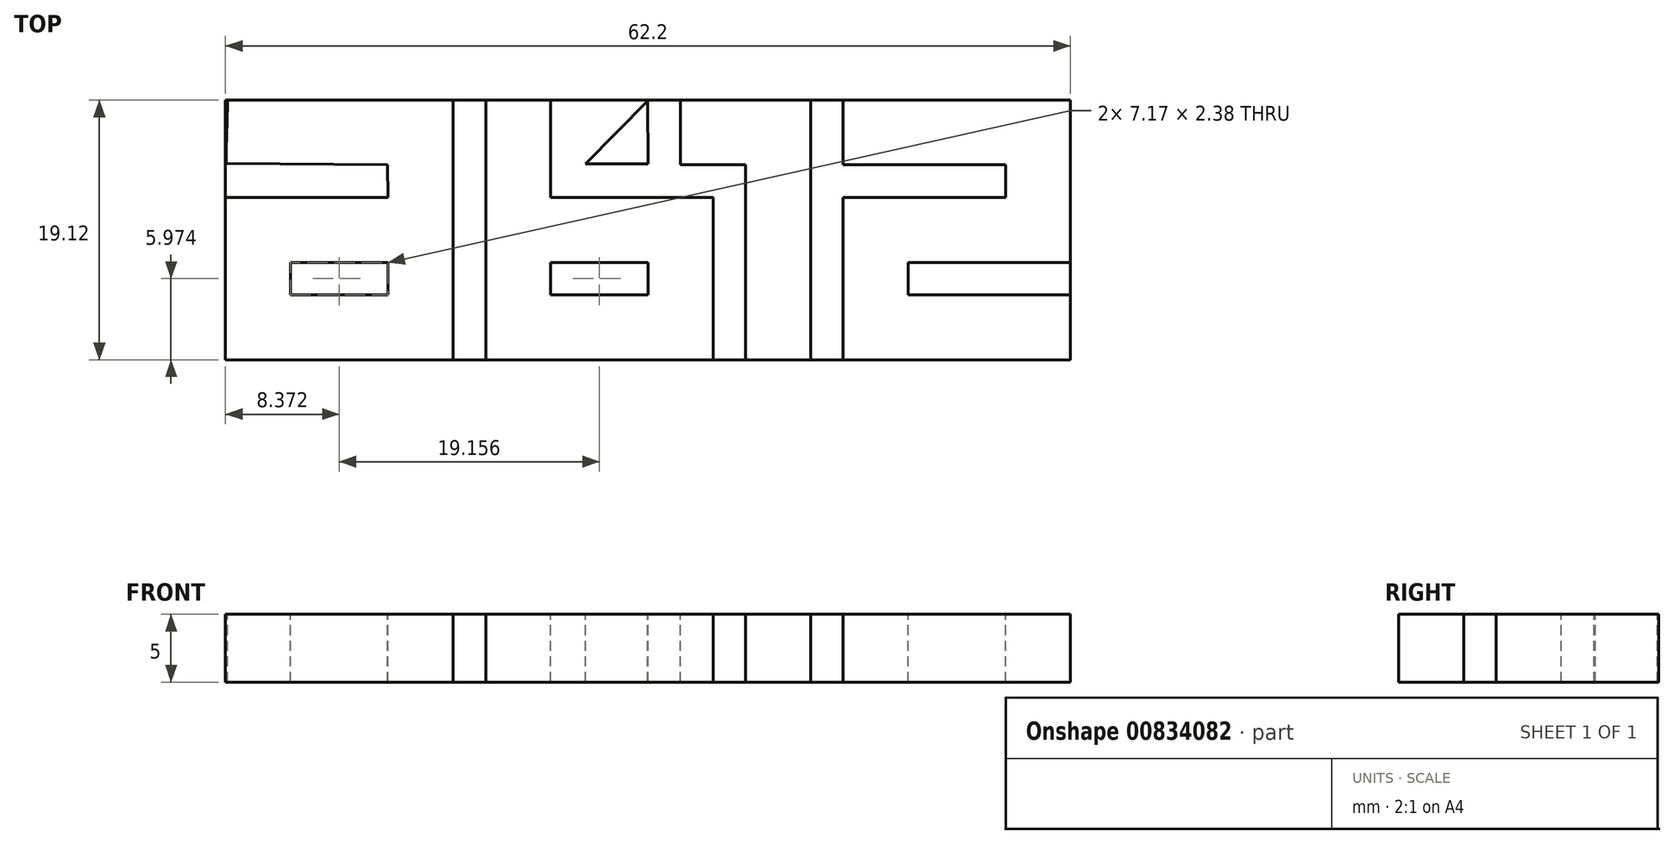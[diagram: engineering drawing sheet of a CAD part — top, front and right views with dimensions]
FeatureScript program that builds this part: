
annotation { "Feature Type Name" : "Feature", "Feature Type Description" : "" }
export const myFeature = defineFeature(function(context is Context, id is Id, definition is map)
    precondition{}
    {
        {
            var Q0;
            Q0=qCreatedBy(makeId("Top.planeOp"),FACE);
            var sketch = newSketch(context, id + "F0", { "sketchPlane" : qUnion([Q0])});
            skLineSegment(sketch, "E0", {"start": v(-31.1, 9.52) * mm, "end": v(-14.35, 9.52) * mm});
            skLineSegment(sketch, "E1", {"start": v(-14.35, 9.52) * mm, "end": v(-14.35, -9.6) * mm});
            skLineSegment(sketch, "E2", {"start": v(-14.35, -9.6) * mm, "end": v(-31.1, -9.6) * mm});
            skLineSegment(sketch, "E3", {"start": v(-31.1, -9.6) * mm, "end": v(-31.1, 2.35) * mm});
            skLineSegment(sketch, "E4", {"start": v(-31.1, 2.35) * mm, "end": v(-19.14, 2.35) * mm});
            skLineSegment(sketch, "E5", {"start": v(-19.14, 2.35) * mm, "end": v(-19.18, 4.77) * mm});
            skLineSegment(sketch, "E6", {"start": v(-19.18, 4.77) * mm, "end": v(-31.06, 4.87) * mm});
            skLineSegment(sketch, "E7", {"start": v(-19.14, -2.44) * mm, "end": v(-26.31, -2.44) * mm});
            skLineSegment(sketch, "E8", {"start": v(-26.31, -2.44) * mm, "end": v(-26.31, -4.82) * mm});
            skLineSegment(sketch, "E9", {"start": v(-26.31, -4.82) * mm, "end": v(-19.14, -4.82) * mm});
            skLineSegment(sketch, "E10", {"start": v(-19.14, -4.82) * mm, "end": v(-19.14, -2.44) * mm});
            skLineSegment(sketch, "E11", {"start": v(-11.95, 9.52) * mm, "end": v(-7.16, 9.52) * mm});
            skLineSegment(sketch, "E12", {"start": v(-7.16, 9.52) * mm, "end": v(-7.16, 2.35) * mm});
            skLineSegment(sketch, "E13", {"start": v(-7.16, 2.35) * mm, "end": v(4.8, 2.35) * mm});
            skLineSegment(sketch, "E14", {"start": v(4.8, 2.35) * mm, "end": v(4.8, -9.6) * mm});
            skLineSegment(sketch, "E15", {"start": v(4.8, -9.6) * mm, "end": v(-11.95, -9.6) * mm});
            skLineSegment(sketch, "E16", {"start": v(-11.95, -9.6) * mm, "end": v(-11.95, 9.52) * mm});
            skLineSegment(sketch, "E17", {"start": v(0.01, -2.44) * mm, "end": v(-7.16, -2.44) * mm});
            skLineSegment(sketch, "E18", {"start": v(-7.16, -2.44) * mm, "end": v(-7.16, -4.82) * mm});
            skLineSegment(sketch, "E19", {"start": v(-7.16, -4.82) * mm, "end": v(0.01, -4.82) * mm});
            skLineSegment(sketch, "E20", {"start": v(0.01, -4.82) * mm, "end": v(0.01, -2.44) * mm});
            skLineSegment(sketch, "E21", {"start": v(7.18, 4.76) * mm, "end": v(7.18, -9.6) * mm});
            skLineSegment(sketch, "E22", {"start": v(7.18, -9.6) * mm, "end": v(11.97, -9.6) * mm});
            skLineSegment(sketch, "E23", {"start": v(11.97, -9.6) * mm, "end": v(11.97, 9.52) * mm});
            skLineSegment(sketch, "E24", {"start": v(11.97, 9.52) * mm, "end": v(2.4, 9.52) * mm});
            skLineSegment(sketch, "E25", {"start": v(2.4, 9.52) * mm, "end": v(2.4, 4.76) * mm});
            skLineSegment(sketch, "E26", {"start": v(2.4, 4.76) * mm, "end": v(7.18, 4.76) * mm});
            skLineSegment(sketch, "E27", {"start": v(31.1, -2.44) * mm, "end": v(19.14, -2.44) * mm});
            skLineSegment(sketch, "E28", {"start": v(19.14, -2.44) * mm, "end": v(19.14, -4.82) * mm});
            skLineSegment(sketch, "E29", {"start": v(19.14, -4.82) * mm, "end": v(31.1, -4.82) * mm});
            skLineSegment(sketch, "E30", {"start": v(31.1, -4.82) * mm, "end": v(31.1, -9.6) * mm});
            skLineSegment(sketch, "E31", {"start": v(31.1, -9.6) * mm, "end": v(14.35, -9.6) * mm});
            skLineSegment(sketch, "E32", {"start": v(14.35, -9.6) * mm, "end": v(14.35, 2.35) * mm});
            skLineSegment(sketch, "E33", {"start": v(14.35, 2.35) * mm, "end": v(26.34, 2.35) * mm});
            skLineSegment(sketch, "E34", {"start": v(26.34, 2.35) * mm, "end": v(26.34, 4.76) * mm});
            skLineSegment(sketch, "E35", {"start": v(26.34, 4.76) * mm, "end": v(14.35, 4.76) * mm});
            skLineSegment(sketch, "E36", {"start": v(14.35, 4.76) * mm, "end": v(14.35, 9.52) * mm});
            skLineSegment(sketch, "E37", {"start": v(14.35, 9.52) * mm, "end": v(31.1, 9.52) * mm});
            skLineSegment(sketch, "E38", {"start": v(31.1, 9.52) * mm, "end": v(31.1, -2.44) * mm});
            skLineSegment(sketch, "E39", {"start": v(-30.95, 9.6) * mm, "end": v(-30.96, 9.21) * mm});
            skLineSegment(sketch, "E40", {"start": v(-30.96, 9.21) * mm, "end": v(-31, 8.03) * mm});
            skLineSegment(sketch, "E41", {"start": v(-31, 8.03) * mm, "end": v(-31.01, 6.85) * mm});
            skLineSegment(sketch, "E42", {"start": v(-31.01, 6.85) * mm, "end": v(-31.03, 6) * mm});
            skLineSegment(sketch, "E43", {"start": v(-31.03, 6) * mm, "end": v(-31.05, 5.44) * mm});
            skLineSegment(sketch, "E44", {"start": v(-31.05, 5.44) * mm, "end": v(-31.05, 5.1) * mm});
            skLineSegment(sketch, "E45", {"start": v(-31.05, 5.1) * mm, "end": v(-31.06, 4.94) * mm});
            skLineSegment(sketch, "E46", {"start": v(-31.06, 4.94) * mm, "end": v(-31.06, 4.88) * mm});
            skLineSegment(sketch, "E47", {"start": v(-31.06, 4.88) * mm, "end": v(-31.06, 4.87) * mm});
            skLineSegment(sketch, "E48", {"start": v(0.01, 4.85) * mm, "end": v(-0.02, 9.45) * mm});
            skLineSegment(sketch, "E49", {"start": v(-0.02, 9.45) * mm, "end": v(-4.6, 4.84) * mm});
            skLineSegment(sketch, "E50", {"start": v(-4.6, 4.84) * mm, "end": v(0.01, 4.85) * mm});
            skSolve(sketch);
        }
        {
            var Q0;
            Q0=makeQuery(id+"F0.imprint","IMPRINT",FACE,{"disambiguationData":[TD([[makeQuery(id+"F0.imprint","IMPRINT",EDGE,{"derivedFrom":sQuery(id+"F0.wireOp",EDGE,"E27")}),-1.0]])]});
            var Q1;
            Q1=makeQuery(id+"F0.imprint","IMPRINT",FACE,{"disambiguationData":[TD([[makeQuery(id+"F0.imprint","IMPRINT",EDGE,{"derivedFrom":sQuery(id+"F0.wireOp",EDGE,"E21")}),1.0]])]});
            var Q2;
            Q2=makeQuery(id+"F0.imprint","IMPRINT",FACE,{"disambiguationData":[TD([[makeQuery(id+"F0.imprint","IMPRINT",EDGE,{"derivedFrom":sQuery(id+"F0.wireOp",EDGE,"E48")}),1.0]])]});
            var Q3;
            Q3=makeQuery(id+"F0.imprint","IMPRINT",FACE,{"disambiguationData":[TD([[makeQuery(id+"F0.imprint","IMPRINT",EDGE,{"derivedFrom":sQuery(id+"F0.wireOp",EDGE,"E11")}),-1.0]])]});
            var Q4;
            {var subQ0=sQuery(id+"F0.wireOp",EDGE,"E1");Q4=makeQuery(id+"F0.imprint","IMPRINT",FACE,{"disambiguationData":[TD([[makeQuery(id+"F0.imprint","IMPRINT",EDGE,{"derivedFrom":subQ0}),-1.0]])]});}
            var Q5;
            Q5=sQuery(id+"F0.wireOp",EDGE,"E31");
            var Q6;
            Q6=sQuery(id+"F0.wireOp",EDGE,"E32");
            var Q7;
            Q7=sQuery(id+"F0.wireOp",EDGE,"E17");
            var Q8;
            Q8=sQuery(id+"F0.wireOp",EDGE,"E27");
            var Q9;
            Q9=sQuery(id+"F0.wireOp",EDGE,"E23");
            var Q10;
            Q10=sQuery(id+"F0.wireOp",EDGE,"E0");
            var Q11;
            Q11=sQuery(id+"F0.wireOp",EDGE,"E9");
            var Q12;
            Q12=sQuery(id+"F0.wireOp",EDGE,"E30");
            var Q13;
            Q13=sQuery(id+"F0.wireOp",EDGE,"E36");
            var Q14;
            Q14=sQuery(id+"F0.wireOp",EDGE,"E33");
            var Q15;
            Q15=sQuery(id+"F0.wireOp",EDGE,"E13");
            var Q16;
            Q16=sQuery(id+"F0.wireOp",EDGE,"E16");
            var Q17;
            Q17=sQuery(id+"F0.wireOp",EDGE,"E15");
            var Q18;
            Q18=sQuery(id+"F0.wireOp",EDGE,"E21");
            var Q19;
            Q19=sQuery(id+"F0.wireOp",EDGE,"E2");
            var Q20;
            Q20=sQuery(id+"F0.wireOp",EDGE,"E24");
            var Q21;
            Q21=sQuery(id+"F0.wireOp",EDGE,"E29");
            var Q22;
            Q22=sQuery(id+"F0.wireOp",EDGE,"E26");
            var Q23;
            Q23=sQuery(id+"F0.wireOp",EDGE,"E4");
            var Q24;
            Q24=sQuery(id+"F0.wireOp",EDGE,"E19");
            var Q25;
            Q25=sQuery(id+"F0.wireOp",EDGE,"E11");
            var Q26;
            Q26=sQuery(id+"F0.wireOp",EDGE,"E14");
            var Q27;
            Q27=sQuery(id+"F0.wireOp",EDGE,"E6");
            var Q28;
            Q28=sQuery(id+"F0.wireOp",EDGE,"E37");
            var Q29;
            Q29=sQuery(id+"F0.wireOp",EDGE,"E35");
            var Q30;
            Q30=sQuery(id+"F0.wireOp",EDGE,"E3");
            var Q31;
            Q31=sQuery(id+"F0.wireOp",EDGE,"E7");
            var Q32;
            Q32=sQuery(id+"F0.wireOp",EDGE,"E25");
            var Q33;
            Q33=sQuery(id+"F0.wireOp",EDGE,"E12");
            var Q34;
            Q34=sQuery(id+"F0.wireOp",EDGE,"E1");
            var Q35;
            Q35=sQuery(id+"F0.wireOp",EDGE,"E38");
            var Q36;
            Q36=sQuery(id+"F0.wireOp",EDGE,"E10");
            var Q37;
            Q37=sQuery(id+"F0.wireOp",EDGE,"E5");
            var Q38;
            Q38=sQuery(id+"F0.wireOp",EDGE,"E28");
            var Q39;
            Q39=sQuery(id+"F0.wireOp",EDGE,"E49");
            var Q40;
            Q40=sQuery(id+"F0.wireOp",EDGE,"E20");
            var Q41;
            Q41=sQuery(id+"F0.wireOp",EDGE,"E48");
            var Q42;
            Q42=sQuery(id+"F0.wireOp",EDGE,"E8");
            var Q43;
            Q43=sQuery(id+"F0.wireOp",EDGE,"E50");
            var Q44;
            Q44=sQuery(id+"F0.wireOp",EDGE,"E22");
            var Q45;
            Q45=sQuery(id+"F0.wireOp",EDGE,"E18");
            var Q46;
            Q46=sQuery(id+"F0.wireOp",EDGE,"E34");
            var Q47;
            Q47=sQuery(id+"F0.wireOp",EDGE,"E39");
            var Q48;
            Q48=sQuery(id+"F0.wireOp",EDGE,"E40");
            var Q49;
            Q49=sQuery(id+"F0.wireOp",EDGE,"E41");
            var Q50;
            Q50=sQuery(id+"F0.wireOp",EDGE,"E43");
            var Q51;
            Q51=sQuery(id+"F0.wireOp",EDGE,"E47");
            var Q52;
            Q52=sQuery(id+"F0.wireOp",EDGE,"E42");
            var Q53;
            Q53=sQuery(id+"F0.wireOp",EDGE,"E44");
            var Q54;
            Q54=sQuery(id+"F0.wireOp",EDGE,"E45");
            var Q55;
            Q55=sQuery(id+"F0.wireOp",EDGE,"E46");
            extrude(context, id + "F1", {"entities" : qUnion([Q0, Q1, Q2, Q3, Q4]), "surfaceEntities" : qUnion([Q5, Q6, Q7, Q8, Q9, Q10, Q11, Q12, Q13, Q14, Q15, Q16, Q17, Q18, Q19, Q20, Q21, Q22, Q23, Q24, Q25, Q26, Q27, Q28, Q29, Q30, Q31, Q32, Q33, Q34, Q35, Q36, Q37, Q38, Q39, Q40, Q41, Q42, Q43, Q44, Q45, Q46, Q47, Q48, Q49, Q50, Q51, Q52, Q53, Q54, Q55]), "oppositeDirection" : true, "depth" : 5 * mm, "offsetDistance" : 25 * mm});
        }
        {
            var Q0;
            Q0=makeQuery(id+"F1.opExtrude","CAP_FACE",FACE,{"disambiguationData":[OSD([sQuery(id+"F0.wireOp",EDGE,"E0"),sQuery(id+"F0.wireOp",EDGE,"E1"),sQuery(id+"F0.wireOp",EDGE,"E2"),sQuery(id+"F0.wireOp",EDGE,"E3"),sQuery(id+"F0.wireOp",EDGE,"E4"),sQuery(id+"F0.wireOp",EDGE,"E5"),sQuery(id+"F0.wireOp",EDGE,"E6"),sQuery(id+"F0.wireOp",EDGE,"E7"),sQuery(id+"F0.wireOp",EDGE,"E8"),sQuery(id+"F0.wireOp",EDGE,"E9"),sQuery(id+"F0.wireOp",EDGE,"E10"),sQuery(id+"F0.wireOp",EDGE,"E39"),sQuery(id+"F0.wireOp",EDGE,"E40"),sQuery(id+"F0.wireOp",EDGE,"E41"),sQuery(id+"F0.wireOp",EDGE,"E42"),sQuery(id+"F0.wireOp",EDGE,"E43"),sQuery(id+"F0.wireOp",EDGE,"E44"),sQuery(id+"F0.wireOp",EDGE,"E45"),sQuery(id+"F0.wireOp",EDGE,"E46"),sQuery(id+"F0.wireOp",EDGE,"E47")])],"isStart":false});
            cPlane(context, id + "F2", {"entities" : qUnion([Q0]), "cplaneType" : CPlaneType.OFFSET, "offset" : 0 * mm, "width" : 150 * mm, "height" : 150 * mm});
        }
        {
            var Q0;
            Q0=qCreatedBy(id+"F2.planeOp",FACE);
            var sketch = newSketch(context, id + "F3", { "sketchPlane" : qUnion([Q0])});
            skLineSegment(sketch, "E51.bottom", {"start": v(-31.1, 9.6) * mm, "end": v(31.1, 9.6) * mm});
            skLineSegment(sketch, "E51.top", {"start": v(-31.1, -9.52) * mm, "end": v(31.1, -9.52) * mm});
            skLineSegment(sketch, "E51.left", {"start": v(-31.1, 9.6) * mm, "end": v(-31.1, -9.52) * mm});
            skLineSegment(sketch, "E51.right", {"start": v(31.1, 9.6) * mm, "end": v(31.1, -9.52) * mm});
            skSolve(sketch);
        }
        {
            var Q0;
            Q0=makeQuery(id+"F3.imprint","IMPRINT",FACE,{"disambiguationData":[TD([[makeQuery(id+"F3.imprint","IMPRINT",EDGE,{"derivedFrom":sQuery(id+"F3.wireOp",EDGE,"E51.bottom")}),-1.0]])]});
            extrude(context, id + "F4", {"entities" : qUnion([Q0]), "oppositeDirection" : true, "depth" : 5 * mm, "offsetDistance" : 25 * mm});
        }
    });
